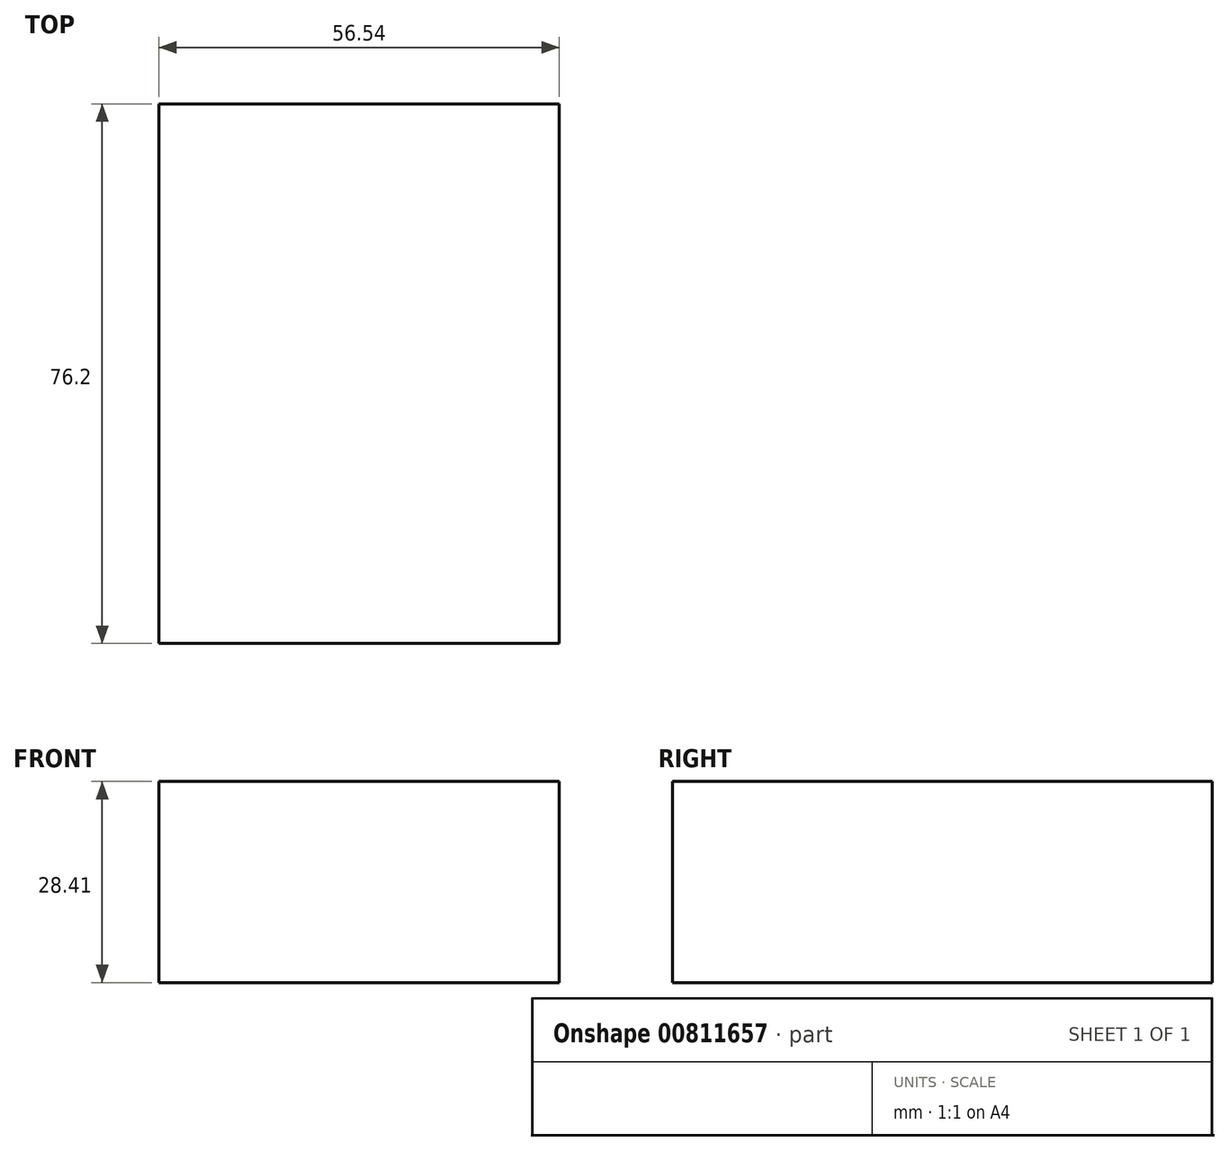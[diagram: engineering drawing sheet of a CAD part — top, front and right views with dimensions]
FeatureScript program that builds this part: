
annotation { "Feature Type Name" : "Feature", "Feature Type Description" : "" }
export const myFeature = defineFeature(function(context is Context, id is Id, definition is map)
    precondition{}
    {
        {
            var Q0;
            Q0=qCreatedBy(makeId("Front.planeOp"),FACE);
            var sketch = newSketch(context, id + "F0", { "sketchPlane" : qUnion([Q0])});
            skLineSegment(sketch, "E0.bottom", {"start": v(0, 0) * mm, "end": v(56.54, 0) * mm});
            skLineSegment(sketch, "E0.top", {"start": v(0, 28.41) * mm, "end": v(56.54, 28.41) * mm});
            skLineSegment(sketch, "E0.left", {"start": v(0, 0) * mm, "end": v(0, 28.41) * mm});
            skLineSegment(sketch, "E0.right", {"start": v(56.54, 0) * mm, "end": v(56.54, 28.41) * mm});
            skSolve(sketch);
        }
        {
            var Q0;
            Q0=makeQuery(id+"F0.imprint","IMPRINT",FACE,{"disambiguationData":[TD([[makeQuery(id+"F0.imprint","IMPRINT",EDGE,{"derivedFrom":sQuery(id+"F0.wireOp",EDGE,"E0.bottom")}),1.0]])]});
            extrude(context, id + "F1", {"entities" : qUnion([Q0]), "depth" : 76.2 * mm, "offsetDistance" : 25.4 * mm});
        }
    });
